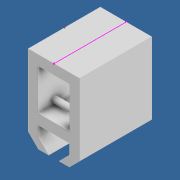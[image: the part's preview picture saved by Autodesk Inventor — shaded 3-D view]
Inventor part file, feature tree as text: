
AUTODESK INVENTOR PART (.ipt)
format: ipt  version: 2020 (Build 240168000, 168)  size: 157,184 bytes
history: native  units: mm
features: sketch x7, extrude x6, chamfer x2
ambient origin geometry x8: Origin, YZ Plane, XZ Plane, XY Plane, X Axis, Y Axis, Z Axis, Center Point
bodies: Solid1 (feature_tree)
feature tree (15):
  extrude  "Extrusion1"  Depth=56.0mm
  extrude  "Extrusion2"  Depth=24.4mm
  extrude  "Extrusion3"  Depth=7.8mm
  extrude  "Extrusion4"  Depth=4.6mm
  sketch  "Sketch14"  dims[d10=4.6mm d11=16.0mm]
  extrude  "Extrusion7"  Depth=16.0mm
  extrude  "Extrusion8"  Depth=26.0mm TaperAngle=0.0deg
  chamfer  "Chamfer1"  Distance=8.0mm
  chamfer  "Chamfer2"  Distance=26.0mm
  sketch  "Sketch1"  dims[d0=39.6mm d1=56.0mm]
  sketch  "Sketch2"  dims[d2=40.0mm d3=0.0mm d4=24.4mm]
  sketch  "Sketch3"  dims[d5=31.8mm d6=7.8mm]
  sketch  "Sketch4"  dims[d7=64.0mm d8=0.0mm d9=4.6mm]
  sketch  "Sketch15"  dims[d12=12.0mm d13=26.0mm d14=0.0mm]
  sketch  "Sketch16"  dims[d15=24.0mm d16=8.0mm d17=26.0mm d18=0.0mm d35=24.0mm d36=0.0mm d37=24.0mm d38=8.0mm d39=8.0mm d40=8.0mm d41=8.0mm d42=8.0mm d43=16.0mm d44=0.0mm d45=0.0mm d46=8.0mm d47=2.0mm d48=45.0deg d49=8.0mm d50=2.0mm d51=45.0deg]
